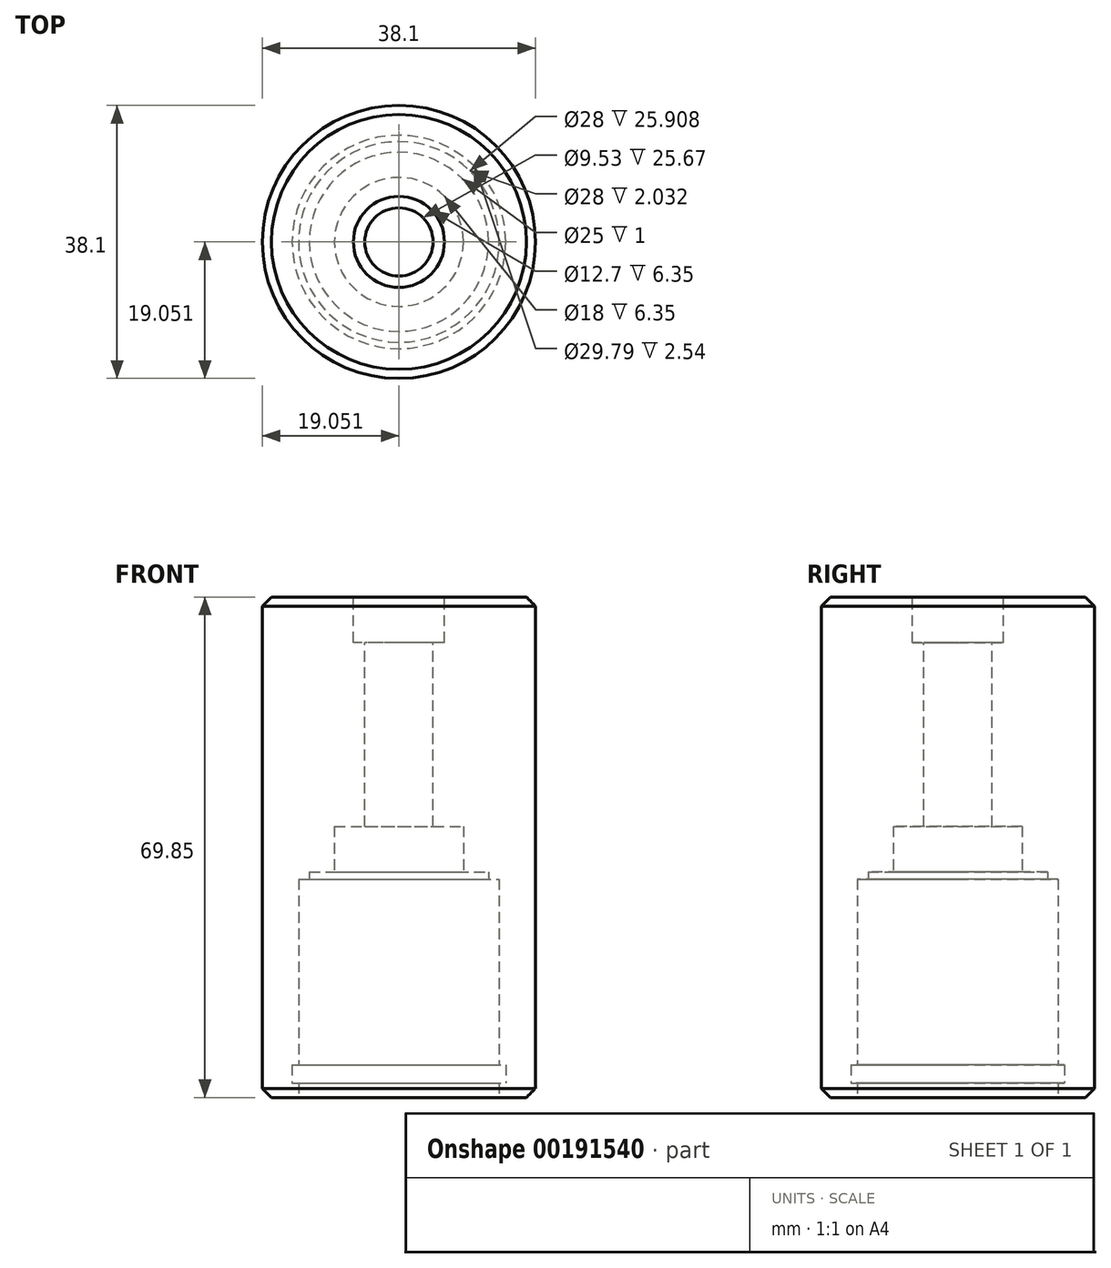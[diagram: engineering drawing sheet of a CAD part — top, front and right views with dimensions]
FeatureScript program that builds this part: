
annotation { "Feature Type Name" : "Feature", "Feature Type Description" : "" }
export const myFeature = defineFeature(function(context is Context, id is Id, definition is map)
    precondition{}
    {
        {
            var Q0;
            Q0=qCreatedBy(makeId("Top.planeOp"),FACE);
            var sketch = newSketch(context, id + "F0", { "sketchPlane" : qUnion([Q0])});
            skCircle(sketch, "E0", {"center": v(-34.2, -25.42) * mm, "radius": 19.05 * mm});
            skSolve(sketch);
        }
        {
            var Q0;
            Q0 = qSketchRegion(id + "F0", true);
            extrude(context, id + "F1", {"entities" : qUnion([Q0]), "depth" : 69.85 * mm});
        }
        {
            var Q0;
            Q0=makeQuery(id+"F1.opExtrude","CAP_FACE",FACE,{"disambiguationData":[OSD([sQuery(id+"F0.wireOp",EDGE,"E0")])],"isStart":true});
            var sketch = newSketch(context, id + "F2", { "sketchPlane" : qUnion([Q0])});
            skCircle(sketch, "E1", {"center": v(-34.2, 25.42) * mm, "radius": 14 * mm});
            skSolve(sketch);
        }
        {
            var Q0;
            Q0 = qSketchRegion(id + "F2", true);
            extrude(context, id + "F3", {"entities" : qUnion([Q0]), "operationType" : NewBodyOperationType.REMOVE, "oppositeDirection" : true, "depth" : 30.48 * mm});
        }
        {
            var Q0;
            Q0=makeQuery(id+"F3.boolean.opBoolean","COPY",FACE,{"derivedFrom":makeQuery(id+"F3.opExtrude","CAP_FACE",FACE,{"disambiguationData":[OSD([sQuery(id+"F2.wireOp",EDGE,"E1")])],"isStart":false})});
            var sketch = newSketch(context, id + "F4", { "sketchPlane" : qUnion([Q0])});
            skCircle(sketch, "E2", {"center": v(-34.2, 25.42) * mm, "radius": 12.5 * mm});
            skSolve(sketch);
        }
        {
            var Q0;
            Q0 = qSketchRegion(id + "F4", true);
            extrude(context, id + "F5", {"entities" : qUnion([Q0]), "operationType" : NewBodyOperationType.REMOVE, "oppositeDirection" : true, "depth" : 1 * mm});
        }
        {
            var Q0;
            Q0=makeQuery(id+"F1.opExtrude","CAP_FACE",FACE,{"disambiguationData":[OSD([sQuery(id+"F0.wireOp",EDGE,"E0")])],"isStart":false});
            var sketch = newSketch(context, id + "F6", { "sketchPlane" : qUnion([Q0])});
            skPoint(sketch, "E3", {"position": v(-34.2, -25.42) * mm});
            skSolve(sketch);
        }
        {
            var Q0;
            Q0=sQuery(id+"F6.wireOp",VERTEX,"E3");
            var Q1;
            Q1=makeQuery(id+"F1.opExtrude","SWEPT_BODY",BODY,{"disambiguationData":[OSD([sQuery(id+"F0.wireOp",EDGE,"E0")])]});
            hole(context, id + "F7", {"style" : HoleStyle.C_BORE, "endStyle" : HoleEndStyle.THROUGH, "holeDiameter" : 9.52 * mm, "cBoreDiameter" : 12.7 * mm, "cBoreDepth" : 6.35 * mm, "startFromSketch" : true, "locations" : qUnion([Q0]), "scope" : qUnion([Q1]), "isTappedThrough" : true});
        }
        {
            var Q0;
            Q0=makeQuery(id+"F5.boolean.opBoolean","COPY",FACE,{"derivedFrom":makeQuery(id+"F5.opExtrude","CAP_FACE",FACE,{"disambiguationData":[OSD([sQuery(id+"F4.wireOp",EDGE,"E2")])],"isStart":false})});
            var sketch = newSketch(context, id + "F8", { "sketchPlane" : qUnion([Q0])});
            skCircle(sketch, "E4", {"center": v(-34.2, 25.42) * mm, "radius": 9 * mm});
            skSolve(sketch);
        }
        {
            var Q0;
            Q0 = qSketchRegion(id + "F8", true);
            extrude(context, id + "F9", {"entities" : qUnion([Q0]), "operationType" : NewBodyOperationType.REMOVE, "oppositeDirection" : true, "depth" : 6.35 * mm});
        }
        {
            var Q0;
            Q0=makeQuery(id+"F3.boolean.opBoolean","COPY",FACE,{"derivedFrom":makeQuery(id+"F3.opExtrude","CAP_FACE",FACE,{"disambiguationData":[OSD([sQuery(id+"F2.wireOp",EDGE,"E1")])],"isStart":false})});
            cPlane(context, id + "F10", {"entities" : qUnion([Q0]), "cplaneType" : CPlaneType.OFFSET, "offset" : 28.45 * mm, "width" : 152.4 * mm, "height" : 152.4 * mm});
        }
        {
            var Q0;
            Q0=qCreatedBy(id+"F10.planeOp",FACE);
            var sketch = newSketch(context, id + "F11", { "sketchPlane" : qUnion([Q0])});
            skCircle(sketch, "E5.0", {"center": v(-34.2, 25.42) * mm, "radius": 14 * mm});
            skCircle(sketch, "E6", {"center": v(-34.2, 25.42) * mm, "radius": 14.9 * mm});
            skSolve(sketch);
        }
        {
            var Q0;
            Q0 = qSketchRegion(id + "F11", true);
            extrude(context, id + "F12", {"entities" : qUnion([Q0]), "operationType" : NewBodyOperationType.REMOVE, "oppositeDirection" : true, "depth" : 2.54 * mm});
        }
        {
            var Q0;
            Q0=makeQuery(id+"F1.opExtrude","CAP_EDGE",EDGE,{"disambiguationData":[OSD([sQuery(id+"F0.wireOp",EDGE,"E0")])],"isStart":false});
            var Q1;
            Q1=makeQuery(id+"F1.opExtrude","CAP_EDGE",EDGE,{"disambiguationData":[OSD([sQuery(id+"F0.wireOp",EDGE,"E0")])],"isStart":true});
            chamfer(context, id + "F13", {"entities" : qUnion([Q0, Q1]), "width" : 1.27 * mm, "tangentPropagation" : true});
        }
    });
